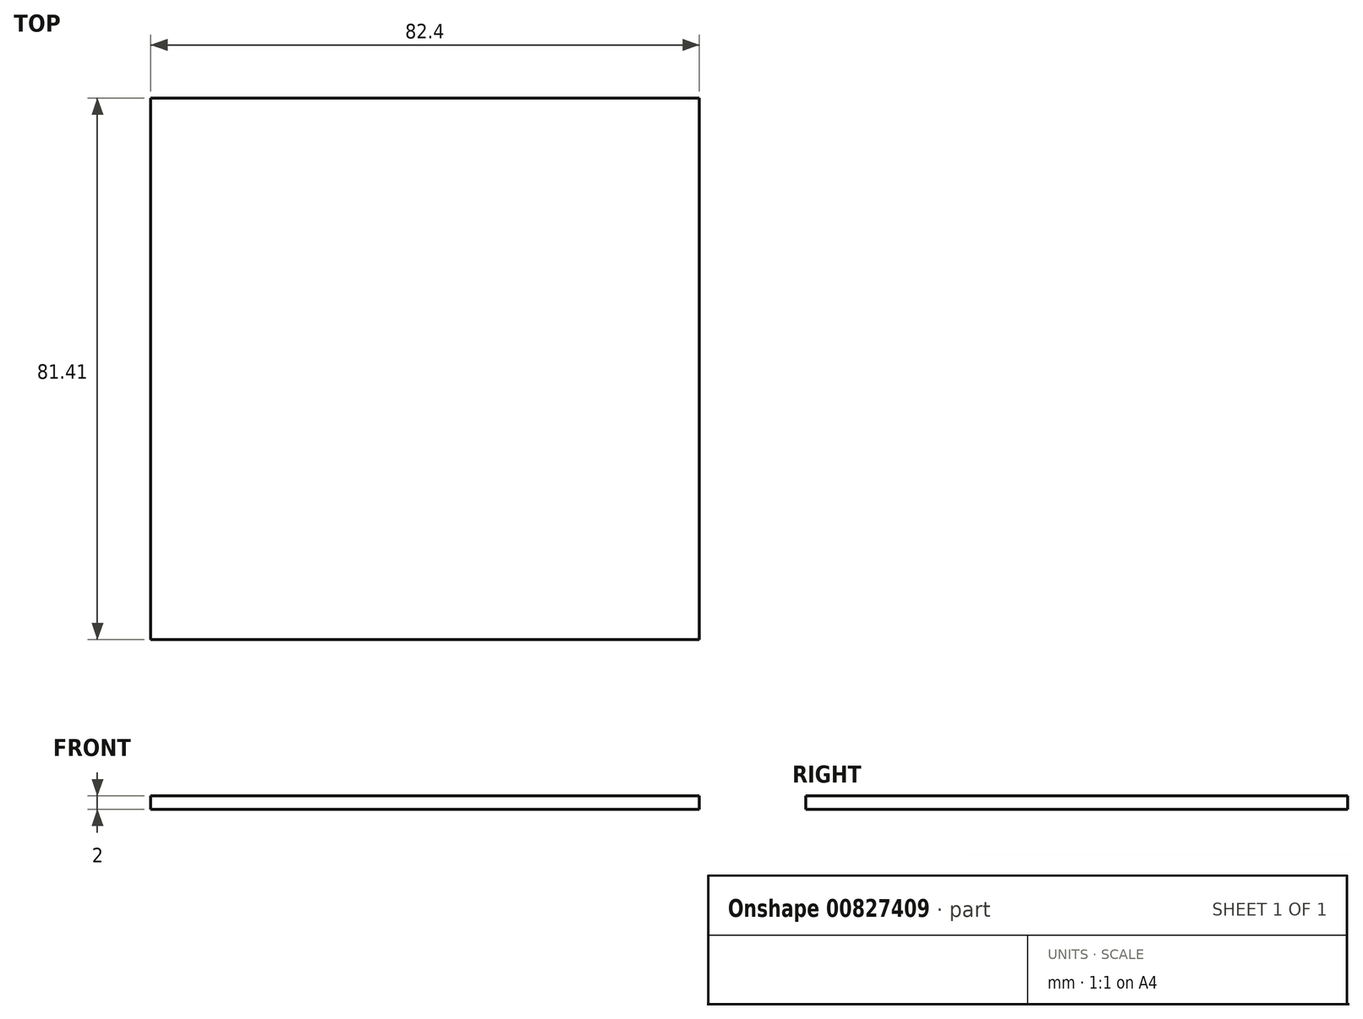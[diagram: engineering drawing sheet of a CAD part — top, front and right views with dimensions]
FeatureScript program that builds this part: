
annotation { "Feature Type Name" : "Feature", "Feature Type Description" : "" }
export const myFeature = defineFeature(function(context is Context, id is Id, definition is map)
    precondition{}
    {
        {
            var Q0;
            Q0=qCreatedBy(makeId("Top.planeOp"),FACE);
            var sketch = newSketch(context, id + "F0", { "sketchPlane" : qUnion([Q0])});
            skLineSegment(sketch, "E0.bottom", {"start": v(-40.31, 41) * mm, "end": v(42.09, 41) * mm});
            skLineSegment(sketch, "E0.top", {"start": v(-40.31, -40.4) * mm, "end": v(42.09, -40.4) * mm});
            skLineSegment(sketch, "E0.left", {"start": v(-40.31, 41) * mm, "end": v(-40.31, -40.4) * mm});
            skLineSegment(sketch, "E0.right", {"start": v(42.09, 41) * mm, "end": v(42.09, -40.4) * mm});
            skSolve(sketch);
        }
        {
            var Q0;
            Q0=makeQuery(id+"F0.imprint","IMPRINT",FACE,{"disambiguationData":[TD([[makeQuery(id+"F0.imprint","IMPRINT",EDGE,{"derivedFrom":sQuery(id+"F0.wireOp",EDGE,"E0.bottom")}),-1.0]])]});
            extrude(context, id + "F1", {"entities" : qUnion([Q0]), "oppositeDirection" : true, "depth" : 2 * mm, "offsetDistance" : 25 * mm});
        }
    });
